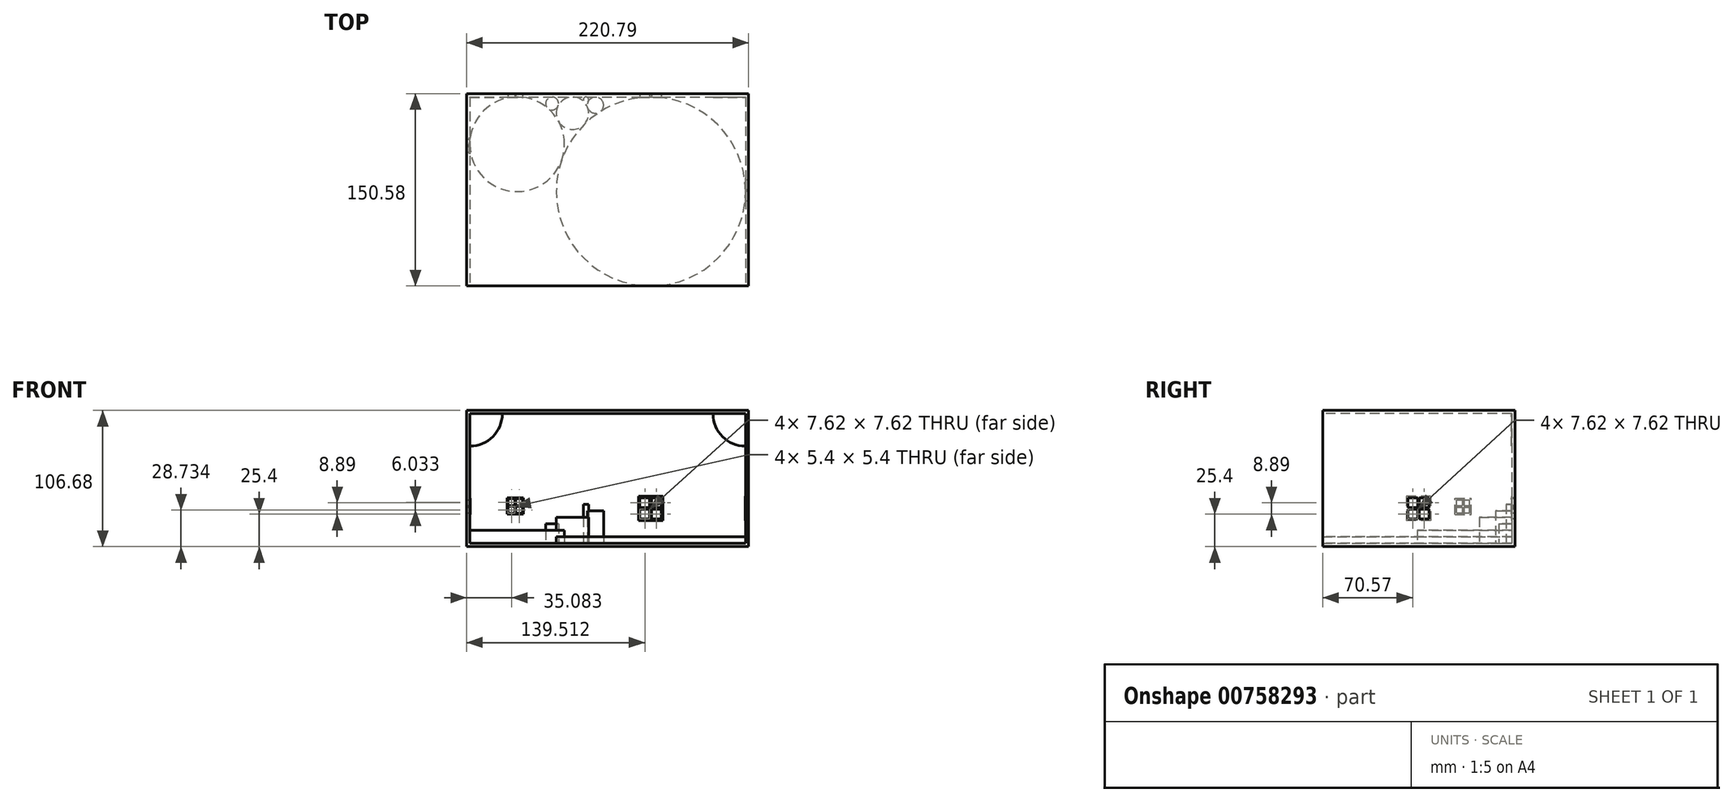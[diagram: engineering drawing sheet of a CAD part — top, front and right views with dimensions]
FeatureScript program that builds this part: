
annotation { "Feature Type Name" : "Feature", "Feature Type Description" : "" }
export const myFeature = defineFeature(function(context is Context, id is Id, definition is map)
    precondition{}
    {
        {
            var Q0;
            Q0=qCreatedBy(makeId("Top.planeOp"),FACE);
            var sketch = newSketch(context, id + "F0", { "sketchPlane" : qUnion([Q0])});
            skCircle(sketch, "E0", {"center": v(0, 0) * mm, "radius": 12.7 * mm});
            skLineSegment(sketch, "E1.bottom", {"start": v(12.7, 12.7) * mm, "end": v(-12.7, 12.7) * mm});
            skLineSegment(sketch, "E1.top", {"start": v(12.7, -12.7) * mm, "end": v(-12.7, -12.7) * mm});
            skLineSegment(sketch, "E1.left", {"start": v(12.7, 12.7) * mm, "end": v(12.7, -12.7) * mm});
            skLineSegment(sketch, "E1.right", {"start": v(-12.7, 12.7) * mm, "end": v(-12.7, -12.7) * mm});
            skCircle(sketch, "E2", {"center": v(10.52, 10.52) * mm, "radius": 2.18 * mm});
            skPoint(sketch, "E2.first.point", {"position": v(10.52, 12.7) * mm});
            skPoint(sketch, "E2.second.point", {"position": v(8.98, 8.98) * mm});
            skPoint(sketch, "E2.third.point", {"position": v(12.7, 10.52) * mm});
            skCircle(sketch, "E3", {"center": v(17.96, 6.35) * mm, "radius": 6.35 * mm});
            skPoint(sketch, "E3.first.point", {"position": v(11.97, 4.23) * mm});
            skPoint(sketch, "E3.second.point", {"position": v(12.42, 9.46) * mm});
            skPoint(sketch, "E3.third.point", {"position": v(22.73, 10.54) * mm});
            skLineSegment(sketch, "E4", {"start": v(91.4, 12.7) * mm, "end": v(-41.74, 12.7) * mm});
            skCircle(sketch, "E5", {"center": v(61.32, -61.32) * mm, "radius": 74.02 * mm});
            skPoint(sketch, "E5.first.point", {"position": v(8.98, -8.98) * mm});
            skPoint(sketch, "E5.second.point", {"position": v(21.39, 1) * mm});
            skPoint(sketch, "E5.third.point", {"position": v(72.48, 11.85) * mm});
            skCircle(sketch, "E6", {"center": v(-43.36, -24.31) * mm, "radius": 37.01 * mm});
            skPoint(sketch, "E6.first.point", {"position": v(-8.47, -36.65) * mm});
            skPoint(sketch, "E6.second.point", {"position": v(-11.08, -6.21) * mm});
            skPoint(sketch, "E6.third.point", {"position": v(-43.36, 12.7) * mm});
            skCircle(sketch, "E7", {"center": v(-16.02, 7.65) * mm, "radius": 5.05 * mm});
            skPoint(sketch, "E7.first.point", {"position": v(-19.3, 3.81) * mm});
            skPoint(sketch, "E7.second.point", {"position": v(-11.46, 5.47) * mm});
            skPoint(sketch, "E7.third.point", {"position": v(-16.02, 12.7) * mm});
            skSolve(sketch);
        }
        {
            var Q0;
            Q0=qCreatedBy(makeId("Top.planeOp"),FACE);
            var sketch = newSketch(context, id + "F1", { "sketchPlane" : qUnion([Q0])});
            skLineSegment(sketch, "E8", {"start": v(-80.37, 12.7) * mm, "end": v(-80.37, -135.34) * mm});
            skLineSegment(sketch, "E9", {"start": v(-80.37, 12.7) * mm, "end": v(135.34, 12.7) * mm});
            skLineSegment(sketch, "E10", {"start": v(135.34, 12.7) * mm, "end": v(135.34, -135.34) * mm});
            skLineSegment(sketch, "E11", {"start": v(-80.37, -135.34) * mm, "end": v(135.34, -135.34) * mm});
            skLineSegment(sketch, "E12", {"start": v(-80.37, -135.34) * mm, "end": v(-82.91, -135.34) * mm});
            skLineSegment(sketch, "E13", {"start": v(-82.91, -135.34) * mm, "end": v(-82.91, 15.24) * mm});
            skLineSegment(sketch, "E14", {"start": v(-82.91, 15.24) * mm, "end": v(137.88, 15.24) * mm});
            skLineSegment(sketch, "E15", {"start": v(137.88, 15.24) * mm, "end": v(137.88, -135.34) * mm});
            skLineSegment(sketch, "E16", {"start": v(137.88, -135.34) * mm, "end": v(135.34, -135.34) * mm});
            skSolve(sketch);
        }
        {
            var Q0;
            Q0=makeQuery(id+"F1.imprint","IMPRINT",FACE,{"disambiguationData":[TD([[makeQuery(id+"F1.imprint","IMPRINT",EDGE,{"derivedFrom":sQuery(id+"F1.wireOp",EDGE,"E8")}),-1.0]])]});
            extrude(context, id + "F2", {"entities" : qUnion([Q0]), "depth" : 101.6 * mm, "offsetDistance" : 25.4 * mm, "hasSecondDirection" : true, "secondDirectionOppositeDirection" : true, "secondDirectionDepth" : 2.54 * mm});
        }
        {
            var Q0;
            Q0=makeQuery(id+"F1.imprint","IMPRINT",FACE,{"disambiguationData":[TD([[makeQuery(id+"F1.imprint","IMPRINT",EDGE,{"derivedFrom":sQuery(id+"F1.wireOp",EDGE,"E8")}),1.0]])]});
            extrude(context, id + "F3", {"entities" : qUnion([Q0]), "operationType" : NewBodyOperationType.ADD, "oppositeDirection" : true, "depth" : 2.54 * mm, "offsetDistance" : 25.4 * mm});
        }
        {
            var Q0;
            {var subQ1=sQuery(id+"F0.wireOp",EDGE,"E1.left");var subQ5=sQuery(id+"F0.wireOp",EDGE,"E1.top");var subQ6=makeQuery(id+"F0.imprint","INTERSECT",VERTEX,{"derivedFrom":[subQ5,subQ1]});Q0=makeQuery(id+"F0.imprint","IMPRINT",FACE,{"disambiguationData":[TD([[makeQuery(id+"F0.imprint","IMPRINT",EDGE,{"disambiguationData":[TD([[subQ6,-1.0]])],"derivedFrom":subQ5}),1.0]])]});}
            var Q1;
            {var subQ0=sQuery(id+"F0.wireOp",EDGE,"E1.left");var subQ1=sQuery(id+"F0.wireOp",EDGE,"E1.top");var subQ2=makeQuery(id+"F0.imprint","INTERSECT",VERTEX,{"derivedFrom":[subQ1,subQ0]});Q1=makeQuery(id+"F0.imprint","IMPRINT",FACE,{"disambiguationData":[TD([[makeQuery(id+"F0.imprint","IMPRINT",EDGE,{"disambiguationData":[TD([[subQ2,-1.0]])],"derivedFrom":subQ1}),-1.0]])]});}
            extrude(context, id + "F4", {"entities" : qUnion([Q0, Q1]), "depth" : 5.08 * mm, "offsetDistance" : 25.4 * mm});
        }
        {
            var Q0;
            {var subQ3=sQuery(id+"F0.wireOp",EDGE,"E1.right");var subQ5=sQuery(id+"F0.wireOp",EDGE,"E1.top");var subQ6=makeQuery(id+"F0.imprint","INTERSECT",VERTEX,{"derivedFrom":[subQ5,subQ3]});Q0=makeQuery(id+"F0.imprint","IMPRINT",FACE,{"disambiguationData":[TD([[makeQuery(id+"F0.imprint","IMPRINT",EDGE,{"disambiguationData":[TD([[subQ6,1.0]])],"derivedFrom":subQ5}),1.0]])]});}
            var Q1;
            {var subQ0=sQuery(id+"F0.wireOp",EDGE,"E1.right");var subQ1=sQuery(id+"F0.wireOp",EDGE,"E1.top");var subQ2=makeQuery(id+"F0.imprint","INTERSECT",VERTEX,{"derivedFrom":[subQ1,subQ0]});Q1=makeQuery(id+"F0.imprint","IMPRINT",FACE,{"disambiguationData":[TD([[makeQuery(id+"F0.imprint","IMPRINT",EDGE,{"disambiguationData":[TD([[subQ2,1.0]])],"derivedFrom":subQ1}),-1.0]])]});}
            extrude(context, id + "F5", {"entities" : qUnion([Q0, Q1]), "depth" : 10.16 * mm, "offsetDistance" : 25.4 * mm});
        }
        {
            var Q0;
            {var subQ0=sQuery(id+"F0.wireOp",EDGE,"E7");var subQ1=sQuery(id+"F0.wireOp",EDGE,"E1.right");var subQ2=makeQuery(id+"F0.imprint","INTERSECT",VERTEX,{"disambiguationData":[OD(0.0)],"derivedFrom":[subQ1,subQ0]});Q0=makeQuery(id+"F0.imprint","IMPRINT",FACE,{"disambiguationData":[TD([[makeQuery(id+"F0.imprint","IMPRINT",EDGE,{"disambiguationData":[TD([[subQ2,-1.0]])],"derivedFrom":subQ1}),1.0]])]});}
            var Q1;
            {var subQ0=sQuery(id+"F0.wireOp",EDGE,"E7");var subQ1=sQuery(id+"F0.wireOp",EDGE,"E1.right");var subQ2=makeQuery(id+"F0.imprint","INTERSECT",VERTEX,{"disambiguationData":[OD(0.0)],"derivedFrom":[subQ1,subQ0]});Q1=makeQuery(id+"F0.imprint","IMPRINT",FACE,{"disambiguationData":[TD([[makeQuery(id+"F0.imprint","IMPRINT",EDGE,{"disambiguationData":[TD([[subQ2,-1.0]])],"derivedFrom":subQ1}),-1.0]])]});}
            extrude(context, id + "F6", {"entities" : qUnion([Q0, Q1]), "depth" : 15.24 * mm, "offsetDistance" : 25.4 * mm});
        }
        {
            var Q0;
            {var subQ0=sQuery(id+"F0.wireOp",EDGE,"E0");var subQ4=makeQuery(id+"F0.imprint","INTERSECT",VERTEX,{"derivedFrom":[subQ0,sQuery(id+"F0.wireOp",EDGE,"E3")]});Q0=makeQuery(id+"F0.imprint","IMPRINT",FACE,{"disambiguationData":[TD([[makeQuery(id+"F0.imprint","IMPRINT",EDGE,{"disambiguationData":[TD([[subQ4,1.0]])],"derivedFrom":subQ0}),1.0]])]});}
            extrude(context, id + "F7", {"entities" : qUnion([Q0]), "depth" : 20.32 * mm, "offsetDistance" : 25.4 * mm});
        }
        {
            var Q0;
            {var subQ0=sQuery(id+"F0.wireOp",EDGE,"E3");var subQ1=sQuery(id+"F0.wireOp",EDGE,"E1.left");var subQ2=makeQuery(id+"F0.imprint","INTERSECT",VERTEX,{"disambiguationData":[OD(0.0)],"derivedFrom":[subQ1,subQ0]});Q0=makeQuery(id+"F0.imprint","IMPRINT",FACE,{"disambiguationData":[TD([[makeQuery(id+"F0.imprint","IMPRINT",EDGE,{"disambiguationData":[TD([[subQ2,-1.0]])],"derivedFrom":subQ1}),1.0]])]});}
            var Q1;
            {var subQ0=sQuery(id+"F0.wireOp",EDGE,"E3");var subQ1=sQuery(id+"F0.wireOp",EDGE,"E1.left");var subQ2=makeQuery(id+"F0.imprint","INTERSECT",VERTEX,{"disambiguationData":[OD(0.0)],"derivedFrom":[subQ1,subQ0]});Q1=makeQuery(id+"F0.imprint","IMPRINT",FACE,{"disambiguationData":[TD([[makeQuery(id+"F0.imprint","IMPRINT",EDGE,{"disambiguationData":[TD([[subQ2,-1.0]])],"derivedFrom":subQ1}),-1.0]])]});}
            extrude(context, id + "F8", {"entities" : qUnion([Q0, Q1]), "depth" : 25.4 * mm, "offsetDistance" : 25.4 * mm});
        }
        {
            var Q0;
            {var subQ0=sQuery(id+"F0.wireOp",EDGE,"E2");var subQ1=makeQuery(id+"F0.imprint","INTERSECT",VERTEX,{"derivedFrom":[subQ0,sQuery(id+"F0.wireOp",EDGE,"E4")]});Q0=makeQuery(id+"F0.imprint","IMPRINT",FACE,{"disambiguationData":[TD([[makeQuery(id+"F0.imprint","IMPRINT",EDGE,{"disambiguationData":[TD([[subQ1,1.0]])],"derivedFrom":subQ0}),1.0]])]});}
            extrude(context, id + "F9", {"entities" : qUnion([Q0]), "depth" : 30.48 * mm, "offsetDistance" : 25.4 * mm});
        }
        {
            var Q0;
            Q0=makeQuery(id+"F1.imprint","IMPRINT",FACE,{"disambiguationData":[TD([[makeQuery(id+"F1.imprint","IMPRINT",EDGE,{"derivedFrom":sQuery(id+"F1.wireOp",EDGE,"E8")}),-1.0]])]});
            var Q1;
            Q1=makeQuery(id+"F1.imprint","IMPRINT",FACE,{"disambiguationData":[TD([[makeQuery(id+"F1.imprint","IMPRINT",EDGE,{"derivedFrom":sQuery(id+"F1.wireOp",EDGE,"E8")}),1.0]])]});
            extrude(context, id + "F10", {"entities" : qUnion([Q0, Q1]), "operationType" : NewBodyOperationType.ADD, "depth" : 104.14 * mm, "offsetDistance" : 25.4 * mm, "hasSecondDirection" : true, "secondDirectionOppositeDirection" : false, "secondDirectionDepth" : 101.6 * mm});
        }
        {
            var Q0;
            Q0=makeQuery(id+"F2.opExtrude","SWEPT_FACE",FACE,{"disambiguationData":[OSD([sQuery(id+"F1.wireOp",EDGE,"E9")])]});
            var sketch = newSketch(context, id + "F11", { "sketchPlane" : qUnion([Q0])});
            skArc(sketch, "E17", {"start": v(-80.37, 76.2) * mm, "mid": v(-62.41, 83.64) * mm, "end": v(-54.97, 101.6) * mm});
            skArc(sketch, "E18", {"start": v(109.94, 101.6) * mm, "mid": v(117.38, 83.64) * mm, "end": v(135.34, 76.2) * mm});
            skLineSegment(sketch, "E19.bottom", {"start": v(51.52, 36.83) * mm, "end": v(70.57, 36.83) * mm});
            skLineSegment(sketch, "E19.top", {"start": v(51.52, 17.78) * mm, "end": v(70.57, 17.78) * mm});
            skLineSegment(sketch, "E19.left", {"start": v(51.52, 36.83) * mm, "end": v(51.52, 17.78) * mm});
            skLineSegment(sketch, "E19.right", {"start": v(70.57, 36.83) * mm, "end": v(70.57, 17.78) * mm});
            skLineSegment(sketch, "E20.bottom", {"start": v(-51.16, 22.86) * mm, "end": v(-38.46, 22.86) * mm});
            skLineSegment(sketch, "E20.top", {"start": v(-51.16, 35.56) * mm, "end": v(-38.46, 35.56) * mm});
            skLineSegment(sketch, "E20.left", {"start": v(-51.16, 22.86) * mm, "end": v(-51.16, 35.56) * mm});
            skLineSegment(sketch, "E20.right", {"start": v(-38.46, 22.86) * mm, "end": v(-38.46, 35.56) * mm});
            skLineSegment(sketch, "E21.bottom", {"start": v(52.8, 35.56) * mm, "end": v(69.3, 35.56) * mm});
            skLineSegment(sketch, "E21.top", {"start": v(52.8, 19.05) * mm, "end": v(69.3, 19.05) * mm});
            skLineSegment(sketch, "E21.left", {"start": v(52.8, 35.56) * mm, "end": v(52.8, 19.05) * mm});
            skLineSegment(sketch, "E21.right", {"start": v(69.3, 35.56) * mm, "end": v(69.3, 19.05) * mm});
            skLineSegment(sketch, "E22", {"start": v(52.8, 27.94) * mm, "end": v(69.3, 27.94) * mm});
            skLineSegment(sketch, "E23", {"start": v(69.3, 26.67) * mm, "end": v(52.8, 26.67) * mm});
            skLineSegment(sketch, "E24", {"start": v(60.41, 35.56) * mm, "end": v(60.41, 19.05) * mm});
            skLineSegment(sketch, "E25", {"start": v(61.68, 19.05) * mm, "end": v(61.68, 35.56) * mm});
            skLineSegment(sketch, "E26.bottom", {"start": v(-50.53, 34.93) * mm, "end": v(-39.1, 34.93) * mm});
            skLineSegment(sketch, "E26.top", {"start": v(-50.53, 23.5) * mm, "end": v(-39.1, 23.5) * mm});
            skLineSegment(sketch, "E26.left", {"start": v(-50.53, 34.93) * mm, "end": v(-50.53, 23.5) * mm});
            skLineSegment(sketch, "E26.right", {"start": v(-39.1, 34.93) * mm, "end": v(-39.1, 23.5) * mm});
            skLineSegment(sketch, "E27.bottom", {"start": v(-50.53, 29.53) * mm, "end": v(-39.1, 29.53) * mm});
            skLineSegment(sketch, "E27.top", {"start": v(-50.53, 28.9) * mm, "end": v(-39.1, 28.9) * mm});
            skLineSegment(sketch, "E27.left", {"start": v(-50.53, 29.53) * mm, "end": v(-50.53, 28.9) * mm});
            skLineSegment(sketch, "E27.right", {"start": v(-39.1, 29.53) * mm, "end": v(-39.1, 28.9) * mm});
            skLineSegment(sketch, "E28.bottom", {"start": v(-45.13, 34.93) * mm, "end": v(-44.5, 34.93) * mm});
            skLineSegment(sketch, "E28.top", {"start": v(-45.13, 23.5) * mm, "end": v(-44.5, 23.5) * mm});
            skLineSegment(sketch, "E28.left", {"start": v(-45.13, 34.93) * mm, "end": v(-45.13, 23.5) * mm});
            skLineSegment(sketch, "E28.right", {"start": v(-44.5, 34.93) * mm, "end": v(-44.5, 23.5) * mm});
            skSolve(sketch);
        }
        {
            var Q0;
            {var subQ0=sQuery(id+"F11.wireOp",EDGE,"E26.left");var subQ1=sQuery(id+"F11.wireOp",EDGE,"E26.bottom");var subQ2=makeQuery(id+"F11.imprint","INTERSECT",VERTEX,{"derivedFrom":[subQ1,subQ0]});Q0=makeQuery(id+"F11.imprint","IMPRINT",FACE,{"disambiguationData":[TD([[makeQuery(id+"F11.imprint","IMPRINT",EDGE,{"disambiguationData":[TD([[subQ2,-1.0]])],"derivedFrom":subQ1}),-1.0]])]});}
            var Q1;
            {var subQ0=sQuery(id+"F11.wireOp",EDGE,"E26.right");var subQ1=sQuery(id+"F11.wireOp",EDGE,"E26.bottom");var subQ2=makeQuery(id+"F11.imprint","INTERSECT",VERTEX,{"derivedFrom":[subQ1,subQ0]});Q1=makeQuery(id+"F11.imprint","IMPRINT",FACE,{"disambiguationData":[TD([[makeQuery(id+"F11.imprint","IMPRINT",EDGE,{"disambiguationData":[TD([[subQ2,1.0]])],"derivedFrom":subQ1}),-1.0]])]});}
            var Q2;
            {var subQ0=sQuery(id+"F11.wireOp",EDGE,"E26.right");var subQ1=sQuery(id+"F11.wireOp",EDGE,"E26.top");var subQ2=makeQuery(id+"F11.imprint","INTERSECT",VERTEX,{"derivedFrom":[subQ1,subQ0]});Q2=makeQuery(id+"F11.imprint","IMPRINT",FACE,{"disambiguationData":[TD([[makeQuery(id+"F11.imprint","IMPRINT",EDGE,{"disambiguationData":[TD([[subQ2,1.0]])],"derivedFrom":subQ1}),1.0]])]});}
            var Q3;
            {var subQ0=sQuery(id+"F11.wireOp",EDGE,"E26.left");var subQ1=sQuery(id+"F11.wireOp",EDGE,"E26.top");var subQ2=makeQuery(id+"F11.imprint","INTERSECT",VERTEX,{"derivedFrom":[subQ1,subQ0]});Q3=makeQuery(id+"F11.imprint","IMPRINT",FACE,{"disambiguationData":[TD([[makeQuery(id+"F11.imprint","IMPRINT",EDGE,{"disambiguationData":[TD([[subQ2,-1.0]])],"derivedFrom":subQ1}),1.0]])]});}
            var Q4;
            {var subQ0=sQuery(id+"F11.wireOp",EDGE,"E21.left");var subQ1=sQuery(id+"F11.wireOp",EDGE,"E21.bottom");var subQ2=makeQuery(id+"F11.imprint","INTERSECT",VERTEX,{"derivedFrom":[subQ1,subQ0]});Q4=makeQuery(id+"F11.imprint","IMPRINT",FACE,{"disambiguationData":[TD([[makeQuery(id+"F11.imprint","IMPRINT",EDGE,{"disambiguationData":[TD([[subQ2,-1.0]])],"derivedFrom":subQ1}),-1.0]])]});}
            var Q5;
            {var subQ0=sQuery(id+"F11.wireOp",EDGE,"E21.left");var subQ1=sQuery(id+"F11.wireOp",EDGE,"E21.top");var subQ2=makeQuery(id+"F11.imprint","INTERSECT",VERTEX,{"derivedFrom":[subQ1,subQ0]});Q5=makeQuery(id+"F11.imprint","IMPRINT",FACE,{"disambiguationData":[TD([[makeQuery(id+"F11.imprint","IMPRINT",EDGE,{"disambiguationData":[TD([[subQ2,-1.0]])],"derivedFrom":subQ1}),1.0]])]});}
            var Q6;
            {var subQ0=sQuery(id+"F11.wireOp",EDGE,"E21.right");var subQ1=sQuery(id+"F11.wireOp",EDGE,"E21.top");var subQ2=makeQuery(id+"F11.imprint","INTERSECT",VERTEX,{"derivedFrom":[subQ1,subQ0]});Q6=makeQuery(id+"F11.imprint","IMPRINT",FACE,{"disambiguationData":[TD([[makeQuery(id+"F11.imprint","IMPRINT",EDGE,{"disambiguationData":[TD([[subQ2,1.0]])],"derivedFrom":subQ1}),1.0]])]});}
            var Q7;
            {var subQ0=sQuery(id+"F11.wireOp",EDGE,"E21.right");var subQ1=sQuery(id+"F11.wireOp",EDGE,"E21.bottom");var subQ2=makeQuery(id+"F11.imprint","INTERSECT",VERTEX,{"derivedFrom":[subQ1,subQ0]});Q7=makeQuery(id+"F11.imprint","IMPRINT",FACE,{"disambiguationData":[TD([[makeQuery(id+"F11.imprint","IMPRINT",EDGE,{"disambiguationData":[TD([[subQ2,1.0]])],"derivedFrom":subQ1}),-1.0]])]});}
            extrude(context, id + "F12", {"entities" : qUnion([Q0, Q1, Q2, Q3, Q4, Q5, Q6, Q7]), "operationType" : NewBodyOperationType.REMOVE, "oppositeDirection" : true, "depth" : 25.4 * mm, "offsetDistance" : 25.4 * mm});
        }
        {
            var Q0;
            {var subQ0=sQuery(id+"F11.wireOp",EDGE,"E17");Q0=makeQuery(id+"F11.imprint","IMPRINT",FACE,{"disambiguationData":[TD([[makeQuery(id+"F11.imprint","IMPRINT",EDGE,{"derivedFrom":subQ0}),1.0]])]});}
            var Q1;
            {var subQ0=sQuery(id+"F11.wireOp",EDGE,"E18");Q1=makeQuery(id+"F11.imprint","IMPRINT",FACE,{"disambiguationData":[TD([[makeQuery(id+"F11.imprint","IMPRINT",EDGE,{"derivedFrom":subQ0}),1.0]])]});}
            var Q2;
            Q2=makeQuery(id+"F11.imprint","IMPRINT",FACE,{"disambiguationData":[TD([[makeQuery(id+"F11.imprint","IMPRINT",EDGE,{"derivedFrom":sQuery(id+"F11.wireOp",EDGE,"E20.bottom")}),1.0]])]});
            var Q3;
            Q3=makeQuery(id+"F11.imprint","IMPRINT",FACE,{"disambiguationData":[TD([[makeQuery(id+"F11.imprint","IMPRINT",EDGE,{"derivedFrom":sQuery(id+"F11.wireOp",EDGE,"E19.bottom")}),-1.0]])]});
            extrude(context, id + "F13", {"entities" : qUnion([Q0, Q1, Q2, Q3]), "depth" : 0.25 * mm, "offsetDistance" : 25.4 * mm});
        }
        {
            var Q0;
            Q0=makeQuery(id+"F3.opExtrude","CAP_FACE",FACE,{"disambiguationData":[OSD([sQuery(id+"F1.wireOp",EDGE,"E8"),sQuery(id+"F1.wireOp",EDGE,"E9"),sQuery(id+"F1.wireOp",EDGE,"E10"),sQuery(id+"F1.wireOp",EDGE,"E11")])],"isStart":true});
            extrude(context, id + "F14", {"entities" : qUnion([Q0]), "depth" : 0.25 * mm, "offsetDistance" : 25.4 * mm});
        }
        {
            var Q0;
            Q0=makeQuery(id+"F2.opExtrude","SWEPT_FACE",FACE,{"disambiguationData":[OSD([sQuery(id+"F1.wireOp",EDGE,"E8")])]});
            var sketch = newSketch(context, id + "F15", { "sketchPlane" : qUnion([Q0])});
            skLineSegment(sketch, "E29.bottom", {"start": v(-31.75, 22.73) * mm, "end": v(-19.05, 22.73) * mm});
            skLineSegment(sketch, "E29.top", {"start": v(-31.75, 35.43) * mm, "end": v(-19.05, 35.43) * mm});
            skLineSegment(sketch, "E29.left", {"start": v(-31.75, 22.73) * mm, "end": v(-31.75, 35.43) * mm});
            skLineSegment(sketch, "E29.right", {"start": v(-19.05, 22.73) * mm, "end": v(-19.05, 35.43) * mm});
            skLineSegment(sketch, "E30.bottom", {"start": v(-30.48, 24) * mm, "end": v(-20.32, 24) * mm});
            skLineSegment(sketch, "E30.top", {"start": v(-30.48, 34.16) * mm, "end": v(-20.32, 34.16) * mm});
            skLineSegment(sketch, "E30.left", {"start": v(-30.48, 24) * mm, "end": v(-30.48, 34.16) * mm});
            skLineSegment(sketch, "E30.right", {"start": v(-20.32, 24) * mm, "end": v(-20.32, 34.16) * mm});
            skLineSegment(sketch, "E31.bottom", {"start": v(-30.48, 29.72) * mm, "end": v(-20.32, 29.72) * mm});
            skLineSegment(sketch, "E31.top", {"start": v(-30.48, 28.45) * mm, "end": v(-20.32, 28.45) * mm});
            skLineSegment(sketch, "E31.left", {"start": v(-30.48, 29.72) * mm, "end": v(-30.48, 28.45) * mm});
            skLineSegment(sketch, "E31.right", {"start": v(-20.32, 29.72) * mm, "end": v(-20.32, 28.45) * mm});
            skLineSegment(sketch, "E32.bottom", {"start": v(-26.04, 34.16) * mm, "end": v(-24.77, 34.16) * mm});
            skLineSegment(sketch, "E32.top", {"start": v(-26.04, 24) * mm, "end": v(-24.77, 24) * mm});
            skLineSegment(sketch, "E32.left", {"start": v(-26.04, 34.16) * mm, "end": v(-26.04, 24) * mm});
            skLineSegment(sketch, "E32.right", {"start": v(-24.77, 34.16) * mm, "end": v(-24.77, 24) * mm});
            skSolve(sketch);
        }
        {
            var Q0;
            Q0=makeQuery(id+"F2.opExtrude","SWEPT_FACE",FACE,{"disambiguationData":[OSD([sQuery(id+"F1.wireOp",EDGE,"E10")])]});
            var sketch = newSketch(context, id + "F16", { "sketchPlane" : qUnion([Q0])});
            skLineSegment(sketch, "E33.bottom", {"start": v(50.8, 36.83) * mm, "end": v(69.85, 36.83) * mm});
            skLineSegment(sketch, "E33.top", {"start": v(50.8, 17.78) * mm, "end": v(69.85, 17.78) * mm});
            skLineSegment(sketch, "E33.left", {"start": v(50.8, 36.83) * mm, "end": v(50.8, 17.78) * mm});
            skLineSegment(sketch, "E33.right", {"start": v(69.85, 36.83) * mm, "end": v(69.85, 17.78) * mm});
            skLineSegment(sketch, "E34.bottom", {"start": v(52.07, 35.56) * mm, "end": v(68.58, 35.56) * mm});
            skLineSegment(sketch, "E34.top", {"start": v(52.07, 19.05) * mm, "end": v(68.58, 19.05) * mm});
            skLineSegment(sketch, "E34.left", {"start": v(52.07, 35.56) * mm, "end": v(52.07, 19.05) * mm});
            skLineSegment(sketch, "E34.right", {"start": v(68.58, 35.56) * mm, "end": v(68.58, 19.05) * mm});
            skLineSegment(sketch, "E35.bottom", {"start": v(52.07, 27.94) * mm, "end": v(68.58, 27.94) * mm});
            skLineSegment(sketch, "E35.top", {"start": v(52.07, 26.67) * mm, "end": v(68.58, 26.67) * mm});
            skLineSegment(sketch, "E35.left", {"start": v(52.07, 27.94) * mm, "end": v(52.07, 26.67) * mm});
            skLineSegment(sketch, "E35.right", {"start": v(68.58, 27.94) * mm, "end": v(68.58, 26.67) * mm});
            skLineSegment(sketch, "E36.bottom", {"start": v(59.69, 35.56) * mm, "end": v(60.96, 35.56) * mm});
            skLineSegment(sketch, "E36.top", {"start": v(59.69, 19.05) * mm, "end": v(60.96, 19.05) * mm});
            skLineSegment(sketch, "E36.left", {"start": v(59.69, 35.56) * mm, "end": v(59.69, 19.05) * mm});
            skLineSegment(sketch, "E36.right", {"start": v(60.96, 35.56) * mm, "end": v(60.96, 19.05) * mm});
            skSolve(sketch);
        }
        {
            var Q0;
            {var subQ0=sQuery(id+"F15.wireOp",EDGE,"E30.left");var subQ1=sQuery(id+"F15.wireOp",EDGE,"E30.top");var subQ2=makeQuery(id+"F15.imprint","INTERSECT",VERTEX,{"derivedFrom":[subQ1,subQ0]});Q0=makeQuery(id+"F15.imprint","IMPRINT",FACE,{"disambiguationData":[TD([[makeQuery(id+"F15.imprint","IMPRINT",EDGE,{"disambiguationData":[TD([[subQ2,-1.0]])],"derivedFrom":subQ1}),-1.0]])]});}
            var Q1;
            {var subQ0=sQuery(id+"F15.wireOp",EDGE,"E30.right");var subQ1=sQuery(id+"F15.wireOp",EDGE,"E30.top");var subQ2=makeQuery(id+"F15.imprint","INTERSECT",VERTEX,{"derivedFrom":[subQ1,subQ0]});Q1=makeQuery(id+"F15.imprint","IMPRINT",FACE,{"disambiguationData":[TD([[makeQuery(id+"F15.imprint","IMPRINT",EDGE,{"disambiguationData":[TD([[subQ2,1.0]])],"derivedFrom":subQ1}),-1.0]])]});}
            var Q2;
            {var subQ0=sQuery(id+"F15.wireOp",EDGE,"E30.right");var subQ1=sQuery(id+"F15.wireOp",EDGE,"E30.bottom");var subQ2=makeQuery(id+"F15.imprint","INTERSECT",VERTEX,{"derivedFrom":[subQ1,subQ0]});Q2=makeQuery(id+"F15.imprint","IMPRINT",FACE,{"disambiguationData":[TD([[makeQuery(id+"F15.imprint","IMPRINT",EDGE,{"disambiguationData":[TD([[subQ2,1.0]])],"derivedFrom":subQ1}),1.0]])]});}
            var Q3;
            {var subQ0=sQuery(id+"F15.wireOp",EDGE,"E30.left");var subQ1=sQuery(id+"F15.wireOp",EDGE,"E30.bottom");var subQ2=makeQuery(id+"F15.imprint","INTERSECT",VERTEX,{"derivedFrom":[subQ1,subQ0]});Q3=makeQuery(id+"F15.imprint","IMPRINT",FACE,{"disambiguationData":[TD([[makeQuery(id+"F15.imprint","IMPRINT",EDGE,{"disambiguationData":[TD([[subQ2,-1.0]])],"derivedFrom":subQ1}),1.0]])]});}
            var Q4;
            {var subQ0=sQuery(id+"F16.wireOp",EDGE,"E34.left");var subQ1=sQuery(id+"F16.wireOp",EDGE,"E34.bottom");var subQ2=makeQuery(id+"F16.imprint","INTERSECT",VERTEX,{"derivedFrom":[subQ1,subQ0]});Q4=makeQuery(id+"F16.imprint","IMPRINT",FACE,{"disambiguationData":[TD([[makeQuery(id+"F16.imprint","IMPRINT",EDGE,{"disambiguationData":[TD([[subQ2,-1.0]])],"derivedFrom":subQ1}),-1.0]])]});}
            var Q5;
            {var subQ0=sQuery(id+"F16.wireOp",EDGE,"E34.right");var subQ1=sQuery(id+"F16.wireOp",EDGE,"E34.bottom");var subQ2=makeQuery(id+"F16.imprint","INTERSECT",VERTEX,{"derivedFrom":[subQ1,subQ0]});Q5=makeQuery(id+"F16.imprint","IMPRINT",FACE,{"disambiguationData":[TD([[makeQuery(id+"F16.imprint","IMPRINT",EDGE,{"disambiguationData":[TD([[subQ2,1.0]])],"derivedFrom":subQ1}),-1.0]])]});}
            var Q6;
            {var subQ0=sQuery(id+"F16.wireOp",EDGE,"E34.right");var subQ1=sQuery(id+"F16.wireOp",EDGE,"E34.top");var subQ2=makeQuery(id+"F16.imprint","INTERSECT",VERTEX,{"derivedFrom":[subQ1,subQ0]});Q6=makeQuery(id+"F16.imprint","IMPRINT",FACE,{"disambiguationData":[TD([[makeQuery(id+"F16.imprint","IMPRINT",EDGE,{"disambiguationData":[TD([[subQ2,1.0]])],"derivedFrom":subQ1}),1.0]])]});}
            var Q7;
            {var subQ0=sQuery(id+"F16.wireOp",EDGE,"E34.left");var subQ1=sQuery(id+"F16.wireOp",EDGE,"E34.top");var subQ2=makeQuery(id+"F16.imprint","INTERSECT",VERTEX,{"derivedFrom":[subQ1,subQ0]});Q7=makeQuery(id+"F16.imprint","IMPRINT",FACE,{"disambiguationData":[TD([[makeQuery(id+"F16.imprint","IMPRINT",EDGE,{"disambiguationData":[TD([[subQ2,-1.0]])],"derivedFrom":subQ1}),1.0]])]});}
            extrude(context, id + "F17", {"entities" : qUnion([Q0, Q1, Q2, Q3, Q4, Q5, Q6, Q7]), "operationType" : NewBodyOperationType.REMOVE, "endBound" : BoundingType.SYMMETRIC, "oppositeDirection" : true, "depth" : 25.4 * mm, "offsetDistance" : 25.4 * mm});
        }
        {
            var Q0;
            Q0=makeQuery(id+"F15.imprint","IMPRINT",FACE,{"disambiguationData":[TD([[makeQuery(id+"F15.imprint","IMPRINT",EDGE,{"derivedFrom":sQuery(id+"F15.wireOp",EDGE,"E29.bottom")}),1.0]])]});
            var Q1;
            Q1=makeQuery(id+"F16.imprint","IMPRINT",FACE,{"disambiguationData":[TD([[makeQuery(id+"F16.imprint","IMPRINT",EDGE,{"derivedFrom":sQuery(id+"F16.wireOp",EDGE,"E33.bottom")}),-1.0]])]});
            extrude(context, id + "F18", {"entities" : qUnion([Q0, Q1]), "endBound" : BoundingType.SYMMETRIC, "depth" : 0.5 * mm, "offsetDistance" : 25.4 * mm});
        }
    });
